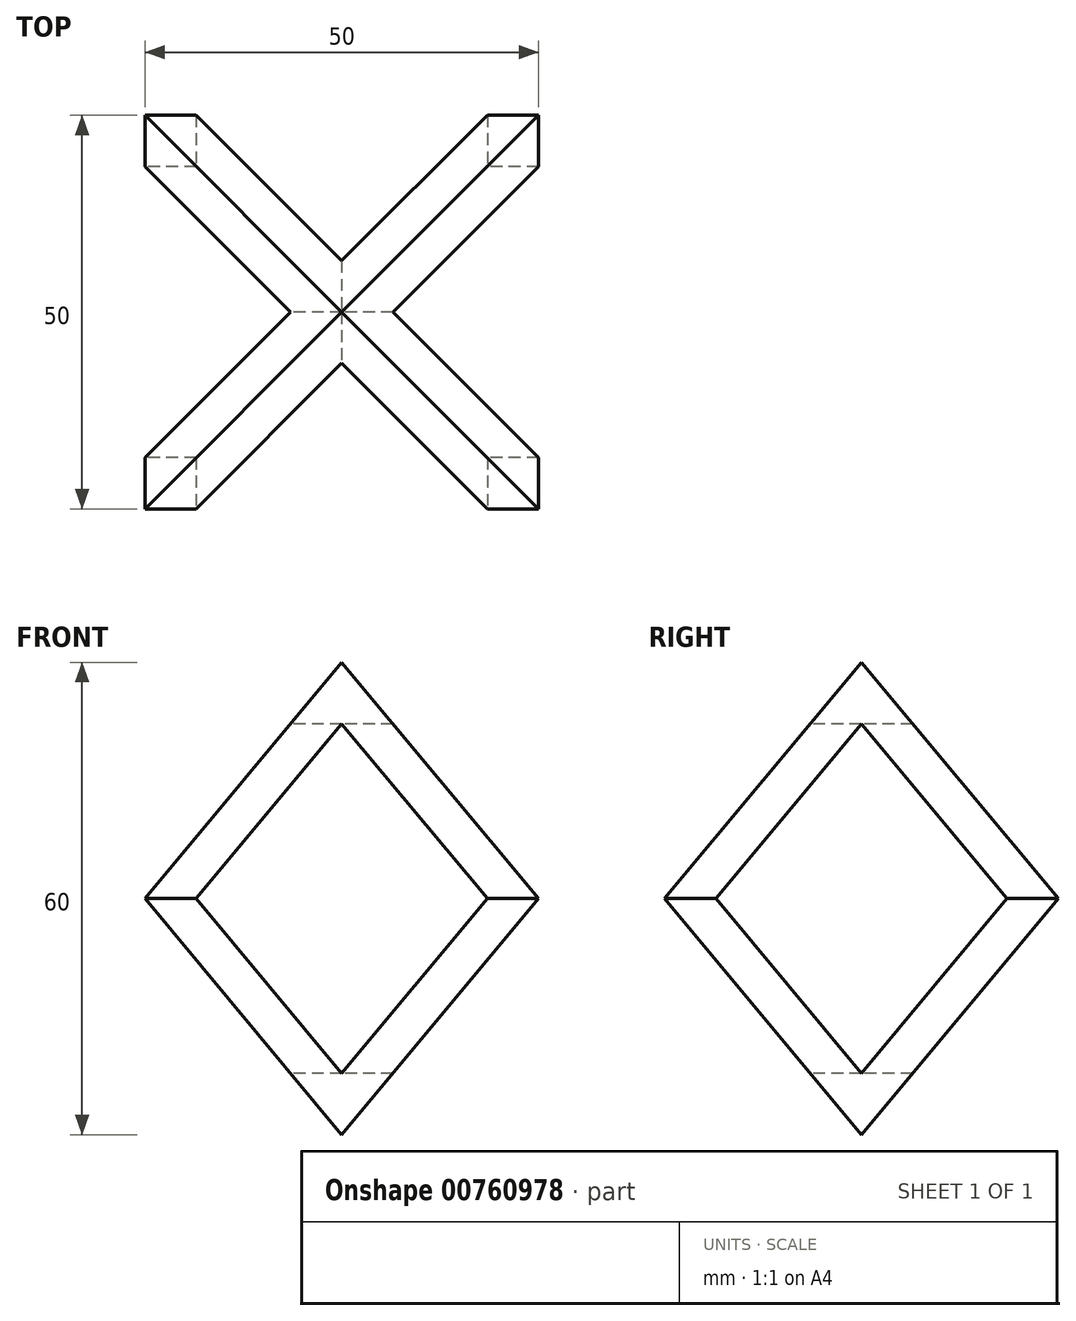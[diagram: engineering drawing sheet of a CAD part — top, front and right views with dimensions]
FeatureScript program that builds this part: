
annotation { "Feature Type Name" : "Feature", "Feature Type Description" : "" }
export const myFeature = defineFeature(function(context is Context, id is Id, definition is map)
    precondition{}
    {
        {
            var Q0;
            Q0=qCreatedBy(makeId("Top.planeOp"),FACE);
            var sketch = newSketch(context, id + "F0", { "sketchPlane" : qUnion([Q0])});
            skLineSegment(sketch, "E0.bottom", {"start": v(0, 0) * mm, "end": v(50, 0) * mm});
            skLineSegment(sketch, "E0.top", {"start": v(0, 50) * mm, "end": v(50, 50) * mm});
            skLineSegment(sketch, "E0.left", {"start": v(0, 0) * mm, "end": v(0, 50) * mm});
            skLineSegment(sketch, "E0.right", {"start": v(50, 0) * mm, "end": v(50, 50) * mm});
            skSolve(sketch);
        }
        {
            var Q0;
            Q0=qSketchRegion(id+"F0",true);
            extrude(context, id + "F1", {"entities" : qUnion([Q0]), "depth" : 60 * mm});
        }
        {
            var Q0;
            Q0=makeQuery(id+"F1.opExtrude","SWEPT_FACE",FACE,{"disambiguationData":[OSD([sQuery(id+"F0.wireOp",EDGE,"E0.bottom")])]});
            var sketch = newSketch(context, id + "F2", { "sketchPlane" : qUnion([Q0])});
            skLineSegment(sketch, "E1", {"start": v(25, 60) * mm, "end": v(0, 30) * mm});
            skLineSegment(sketch, "E2", {"start": v(0, 30) * mm, "end": v(25, 0) * mm});
            skLineSegment(sketch, "E3", {"start": v(25, 0) * mm, "end": v(50, 30) * mm});
            skLineSegment(sketch, "E4", {"start": v(50, 30) * mm, "end": v(25, 60) * mm});
            skLineSegment(sketch, "E5", {"start": v(6.5, 30) * mm, "end": v(25, 52.19) * mm});
            skLineSegment(sketch, "E6", {"start": v(25, 52.19) * mm, "end": v(43.5, 30) * mm});
            skLineSegment(sketch, "E7", {"start": v(43.5, 30) * mm, "end": v(25, 7.81) * mm});
            skLineSegment(sketch, "E8", {"start": v(25, 7.81) * mm, "end": v(6.5, 30) * mm});
            skLineSegment(sketch, "E9", {"start": v(11.8, 44.17) * mm, "end": v(15.65, 40.96) * mm, "construction": true});
            skSolve(sketch);
        }
        {
            var Q0;
            Q0=makeQuery(id+"F1.opExtrude","SWEPT_FACE",FACE,{"disambiguationData":[OSD([sQuery(id+"F0.wireOp",EDGE,"E0.left")])]});
            var sketch = newSketch(context, id + "F3", { "sketchPlane" : qUnion([Q0])});
            skLineSegment(sketch, "E10", {"start": v(-25, 0) * mm, "end": v(-50, 30) * mm});
            skLineSegment(sketch, "E11", {"start": v(-50, 30) * mm, "end": v(-25, 60) * mm});
            skLineSegment(sketch, "E12", {"start": v(-25, 60) * mm, "end": v(0, 30) * mm});
            skLineSegment(sketch, "E13", {"start": v(0, 30) * mm, "end": v(-25, 0) * mm});
            skLineSegment(sketch, "E14", {"start": v(-25, 7.81) * mm, "end": v(-43.5, 30) * mm});
            skLineSegment(sketch, "E15", {"start": v(-43.5, 30) * mm, "end": v(-25, 52.19) * mm});
            skLineSegment(sketch, "E16", {"start": v(-25, 52.19) * mm, "end": v(-6.5, 30) * mm});
            skLineSegment(sketch, "E17", {"start": v(-6.5, 30) * mm, "end": v(-25, 7.81) * mm});
            skLineSegment(sketch, "E18", {"start": v(-40.06, 41.93) * mm, "end": v(-36.22, 38.73) * mm, "construction": true});
            skSolve(sketch);
        }
        {
            var Q0;
            Q0=qSketchRegion(id+"F2",true);
            extrude(context, id + "F4", {"entities" : qUnion([Q0]), "operationType" : NewBodyOperationType.INTERSECT, "endBound" : BoundingType.THROUGH_ALL, "oppositeDirection" : true, "depth" : 25 * mm});
        }
        {
            var Q0;
            Q0=qSketchRegion(id+"F3",true);
            extrude(context, id + "F5", {"entities" : qUnion([Q0]), "operationType" : NewBodyOperationType.INTERSECT, "endBound" : BoundingType.THROUGH_ALL, "oppositeDirection" : true, "depth" : 25 * mm});
        }
    });
